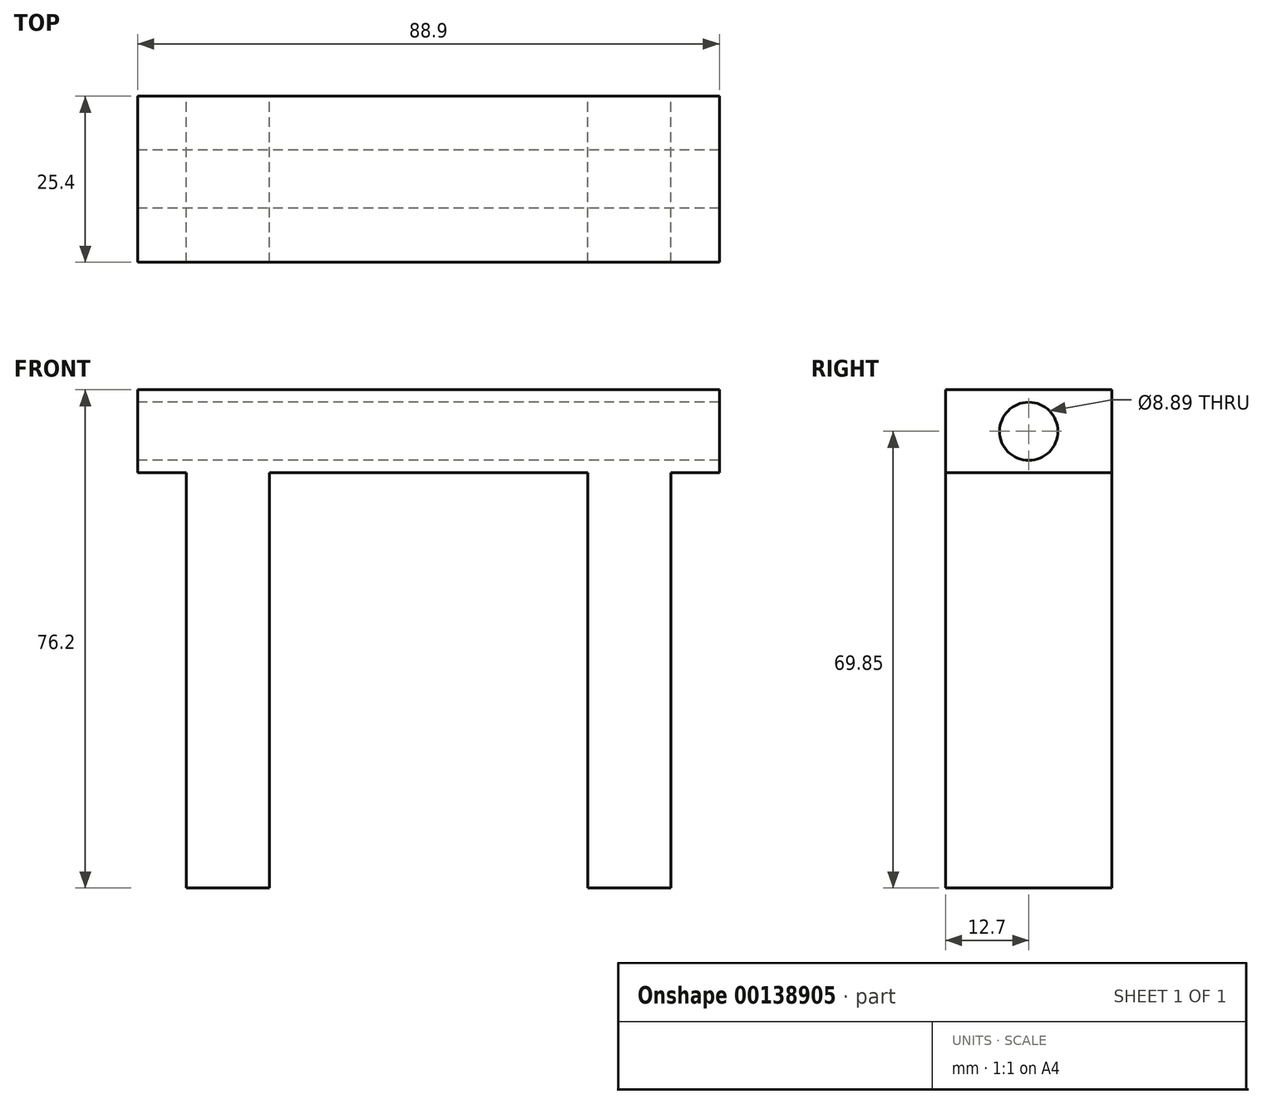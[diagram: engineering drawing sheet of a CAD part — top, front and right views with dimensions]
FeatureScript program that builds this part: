
annotation { "Feature Type Name" : "Feature", "Feature Type Description" : "" }
export const myFeature = defineFeature(function(context is Context, id is Id, definition is map)
    precondition{}
    {
        {
            var Q0;
            Q0=qCreatedBy(makeId("Front.planeOp"),FACE);
            var sketch = newSketch(context, id + "F0", { "sketchPlane" : qUnion([Q0])});
            skLineSegment(sketch, "E0.bottom", {"start": v(44.45, -6.35) * mm, "end": v(-44.45, -6.35) * mm});
            skLineSegment(sketch, "E0.top", {"start": v(44.45, 6.35) * mm, "end": v(-44.45, 6.35) * mm});
            skLineSegment(sketch, "E0.left", {"start": v(44.45, -6.35) * mm, "end": v(44.45, 6.35) * mm});
            skLineSegment(sketch, "E0.right", {"start": v(-44.45, -6.35) * mm, "end": v(-44.45, 6.35) * mm});
            skPoint(sketch, "E0.middle", {"position": v(0, 0) * mm});
            skLineSegment(sketch, "E1", {"start": v(-37.03, -6.35) * mm, "end": v(-37.03, -69.85) * mm});
            skLineSegment(sketch, "E2", {"start": v(-37.03, -69.85) * mm, "end": v(-24.33, -69.85) * mm});
            skLineSegment(sketch, "E3", {"start": v(-24.33, -69.85) * mm, "end": v(-24.33, -6.35) * mm});
            skLineSegment(sketch, "E4.MirrorCS", {"start": v(37.03, -6.35) * mm, "end": v(37.03, -69.85) * mm});
            skLineSegment(sketch, "E5.MirrorCS", {"start": v(24.33, -69.85) * mm, "end": v(24.33, -6.35) * mm});
            skLineSegment(sketch, "E6.MirrorCS", {"start": v(37.03, -69.85) * mm, "end": v(24.33, -69.85) * mm});
            skSolve(sketch);
        }
        {
            var Q0;
            Q0 = qSketchRegion(id + "F0", true);
            extrude(context, id + "F1", {"entities" : qUnion([Q0]), "depth" : 25.4 * mm});
        }
        {
            var Q0;
            Q0=makeQuery(id+"F1.opExtrude","SWEPT_FACE",FACE,{"disambiguationData":[OSD([sQuery(id+"F0.wireOp",EDGE,"E0.right")])]});
            var sketch = newSketch(context, id + "F2", { "sketchPlane" : qUnion([Q0])});
            skCircle(sketch, "E7", {"center": v(12.7, 0) * mm, "radius": 4.45 * mm});
            skPoint(sketch, "E7.centerSnap0", {"position": v(12.7, 6.35) * mm});
            skSolve(sketch);
        }
        {
            var Q0;
            Q0 = qSketchRegion(id + "F2", true);
            extrude(context, id + "F3", {"entities" : qUnion([Q0]), "operationType" : NewBodyOperationType.REMOVE, "endBound" : BoundingType.THROUGH_ALL, "oppositeDirection" : true, "depth" : 25.4 * mm});
        }
    });
